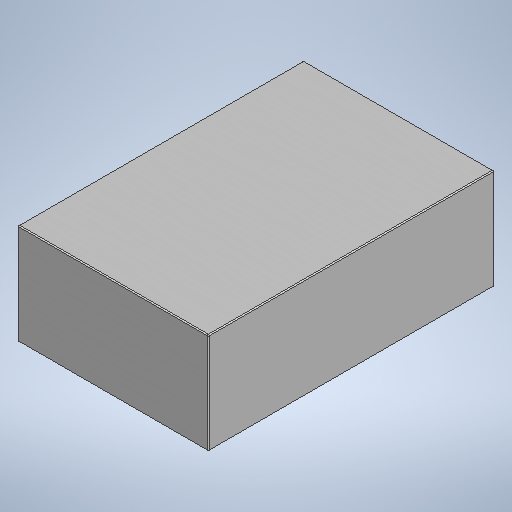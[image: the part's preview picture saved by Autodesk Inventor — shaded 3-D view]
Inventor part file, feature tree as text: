
AUTODESK INVENTOR PART (.ipt)
format: ipt  version: 2025 (Build 290162000, 162)  size: 233,984 bytes
history: native  units: in
note: dims shown in document units (in); Inventor stores cm internally (conversion verified against a paired STEP export)
features: other x2, extrude x1, fillet x1, sketch x1
ambient origin geometry x8: Origin, YZ Plane, XZ Plane, XY Plane, X Axis, Y Axis, Z Axis, Center Point
bodies: Solid1 (feature_tree)
feature tree (5):
  extrude  "Extrusion1"  Depth=15.748in
  fillet  "Fillet1"  Radius=23.622in
  sketch  "Sketch1"  dims[d0=8.3331in d1=15.748in d2=23.622in d3=0.0in d4=0.0787in]
  other  "Finish1"
  other  "Finish2"
